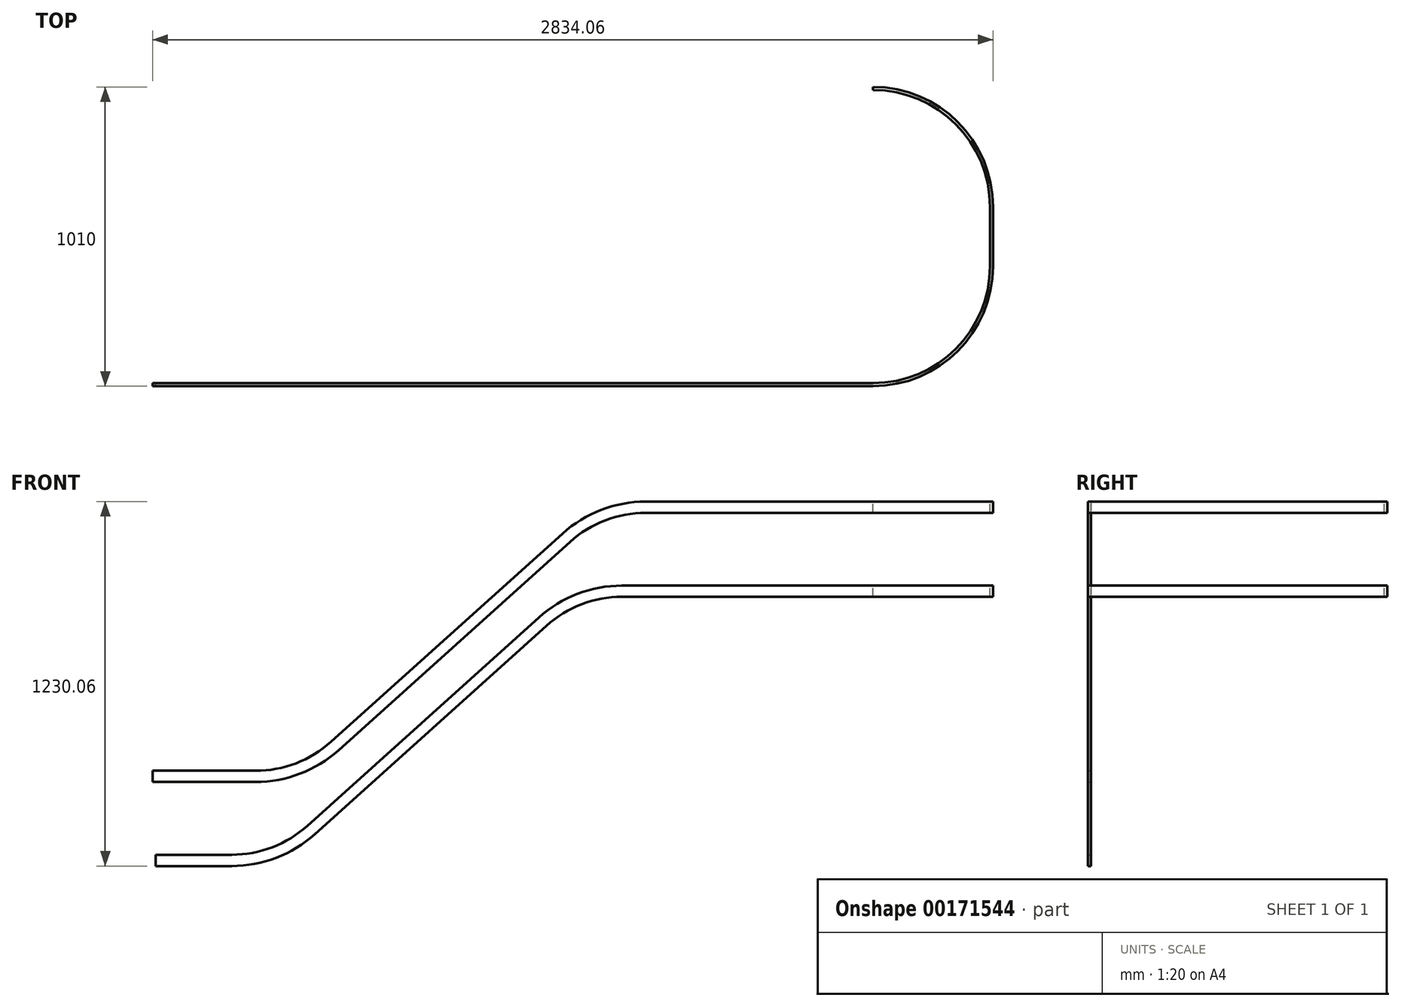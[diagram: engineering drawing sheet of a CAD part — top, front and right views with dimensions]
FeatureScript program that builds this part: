
annotation { "Feature Type Name" : "Feature", "Feature Type Description" : "" }
export const myFeature = defineFeature(function(context is Context, id is Id, definition is map)
    precondition{}
    {
        {
            var Q0;
            Q0=qCreatedBy(makeId("Front.planeOp"),FACE);
            var sketch = newSketch(context, id + "F0", { "sketchPlane" : qUnion([Q0])});
            skLineSegment(sketch, "E0", {"start": v(129.67, 109.8) * mm, "end": v(910.51, 812.88) * mm, "construction": true});
            skArc(sketch, "E1.0", {"start": v(1191.37, 1269.69) * mm, "mid": v(1191.37, 1269.69) * mm, "end": v(1191.36, 1269.69) * mm});
            skLineSegment(sketch, "E2", {"start": v(1191.36, 1269.69) * mm, "end": v(1191.37, 1269.69) * mm});
            skLineSegment(sketch, "E3", {"start": v(-404.44, 290.56) * mm, "end": v(-57.98, 290.56) * mm, "construction": true});
            skLineSegment(sketch, "E4", {"start": v(-394.44, 7.06) * mm, "end": v(-137.98, 7.06) * mm, "construction": true});
            skLineSegment(sketch, "E5", {"start": v(1178.16, 915.62) * mm, "end": v(2024.62, 915.62) * mm, "construction": true});
            skLineSegment(sketch, "E6", {"start": v(1258.16, 1199.12) * mm, "end": v(2024.62, 1199.12) * mm, "construction": true});
            skPoint(sketch, "E7", {"position": v(-404.44, 309.56) * mm});
            skPoint(sketch, "E8", {"position": v(-404.44, 271.56) * mm});
            skPoint(sketch, "E9", {"position": v(-394.44, 26.06) * mm});
            skPoint(sketch, "E10", {"position": v(-394.44, -11.94) * mm});
            skPoint(sketch, "E11", {"position": v(2024.62, 896.62) * mm});
            skPoint(sketch, "E12", {"position": v(2024.62, 934.62) * mm});
            skPoint(sketch, "E13.visualSharp", {"position": v(95.56, 290.56) * mm});
            skPoint(sketch, "E14.visualSharp", {"position": v(15.56, 7.06) * mm});
            skPoint(sketch, "E15.visualSharp", {"position": v(1024.62, 915.62) * mm});
            skPoint(sketch, "E16.visualSharp", {"position": v(1104.62, 1199.12) * mm});
            skLineSegment(sketch, "E17", {"start": v(-404.44, 271.56) * mm, "end": v(-404.44, 309.56) * mm});
            skLineSegment(sketch, "E18", {"start": v(-394.44, 26.06) * mm, "end": v(-394.44, -11.94) * mm});
            skLineSegment(sketch, "E19", {"start": v(2024.62, 896.62) * mm, "end": v(2024.62, 934.62) * mm});
            skLineSegment(sketch, "E20", {"start": v(572.56, 720.05) * mm, "end": v(572.56, 508.58) * mm, "construction": true});
            skLineSegment(sketch, "E21", {"start": v(209.67, 393.3) * mm, "end": v(990.51, 1096.38) * mm, "construction": true});
            skArc(sketch, "E22.filletArc", {"start": v(-137.98, 7.06) * mm, "mid": v(5.37, 33.63) * mm, "end": v(129.67, 109.8) * mm, "construction": true});
            skArc(sketch, "E23.filletArc", {"start": v(-57.98, 290.56) * mm, "mid": v(85.37, 317.13) * mm, "end": v(209.67, 393.3) * mm, "construction": true});
            skArc(sketch, "E24.filletArc", {"start": v(1178.16, 915.62) * mm, "mid": v(1034.82, 889.05) * mm, "end": v(910.51, 812.88) * mm, "construction": true});
            skArc(sketch, "E25.filletArc", {"start": v(1258.16, 1199.12) * mm, "mid": v(1114.82, 1172.55) * mm, "end": v(990.51, 1096.38) * mm, "construction": true});
            skArc(sketch, "E26.0", {"start": v(-137.98, -11.94) * mm, "mid": v(12.18, 15.9) * mm, "end": v(142.39, 95.69) * mm});
            skArc(sketch, "E27.0", {"start": v(-137.98, 26.06) * mm, "mid": v(-1.44, 51.37) * mm, "end": v(116.96, 123.93) * mm});
            skArc(sketch, "E28.0", {"start": v(1178.16, 934.62) * mm, "mid": v(1028, 906.8) * mm, "end": v(897.8, 827) * mm});
            skArc(sketch, "E29.0", {"start": v(1178.16, 896.62) * mm, "mid": v(1041.63, 871.31) * mm, "end": v(923.23, 798.76) * mm});
            skArc(sketch, "E30.0", {"start": v(1258.16, 1218.12) * mm, "mid": v(1108, 1190.3) * mm, "end": v(977.8, 1110.5) * mm});
            skArc(sketch, "E31.0", {"start": v(1258.16, 1180.12) * mm, "mid": v(1121.63, 1154.81) * mm, "end": v(1003.23, 1082.26) * mm});
            skArc(sketch, "E32.0", {"start": v(-57.98, 271.56) * mm, "mid": v(92.18, 299.4) * mm, "end": v(222.39, 379.19) * mm});
            skArc(sketch, "E33.0", {"start": v(-57.98, 309.56) * mm, "mid": v(78.56, 334.87) * mm, "end": v(196.96, 407.43) * mm});
            skLineSegment(sketch, "E34", {"start": v(-57.98, 271.56) * mm, "end": v(-404.44, 271.56) * mm});
            skLineSegment(sketch, "E35", {"start": v(-57.98, 309.56) * mm, "end": v(-404.44, 309.56) * mm});
            skLineSegment(sketch, "E36", {"start": v(222.39, 379.19) * mm, "end": v(1003.23, 1082.26) * mm});
            skLineSegment(sketch, "E37", {"start": v(196.96, 407.43) * mm, "end": v(977.8, 1110.5) * mm});
            skLineSegment(sketch, "E38", {"start": v(-137.98, -11.94) * mm, "end": v(-394.44, -11.94) * mm});
            skLineSegment(sketch, "E39", {"start": v(-394.44, 26.06) * mm, "end": v(-137.98, 26.06) * mm});
            skLineSegment(sketch, "E40", {"start": v(142.39, 95.69) * mm, "end": v(923.23, 798.76) * mm});
            skLineSegment(sketch, "E41", {"start": v(897.8, 827) * mm, "end": v(116.96, 123.93) * mm});
            skLineSegment(sketch, "E42", {"start": v(1178.16, 896.62) * mm, "end": v(2024.62, 896.62) * mm});
            skLineSegment(sketch, "E43", {"start": v(2024.62, 934.62) * mm, "end": v(1178.16, 934.62) * mm});
            skLineSegment(sketch, "E44", {"start": v(1258.16, 1180.12) * mm, "end": v(2024.62, 1180.12) * mm});
            skLineSegment(sketch, "E45", {"start": v(2024.62, 1218.12) * mm, "end": v(1258.16, 1218.12) * mm});
            skLineSegment(sketch, "E46", {"start": v(2024.62, 1180.12) * mm, "end": v(2024.62, 1218.12) * mm});
            skSolve(sketch);
        }
        {
            var Q0;
            Q0=qSketchRegion(id+"F0",true);
            extrude(context, id + "F1", {"entities" : qUnion([Q0]), "depth" : 10 * mm});
        }
        {
            var Q0;
            Q0=makeQuery(id+"F1.opExtrude","SWEPT_FACE",FACE,{"disambiguationData":[OSD([sQuery(id+"F0.wireOp",EDGE,"E45")])]});
            var sketch = newSketch(context, id + "F2", { "sketchPlane" : qUnion([Q0])});
            skLineSegment(sketch, "E47", {"start": v(2024.62, -5) * mm, "end": v(2024.62, 795) * mm, "construction": true});
            skArc(sketch, "E48", {"start": v(2024.62, -5) * mm, "mid": v(2307.46, 112.16) * mm, "end": v(2424.62, 395) * mm});
            skLineSegment(sketch, "E49", {"start": v(2024.62, 795) * mm, "end": v(2024.62, 995) * mm, "construction": true});
            skLineSegment(sketch, "E50", {"start": v(2424.62, 595) * mm, "end": v(2424.62, 995) * mm, "construction": true});
            skArc(sketch, "E51", {"start": v(2424.62, 595) * mm, "mid": v(2307.46, 877.84) * mm, "end": v(2024.62, 995) * mm});
            skPoint(sketch, "E51.second.point", {"position": v(2424.62, 595) * mm});
            skPoint(sketch, "E51.third.point", {"position": v(1768.82, 287.49) * mm});
            skLineSegment(sketch, "E52", {"start": v(2424.62, 595) * mm, "end": v(2424.62, 395) * mm});
            skSolve(sketch);
        }
        {
            var Q0;
            Q0=makeQuery(id+"F1.opExtrude","SWEPT_FACE",FACE,{"disambiguationData":[OSD([sQuery(id+"F0.wireOp",EDGE,"E46")])]});
            var Q1;
            Q1=sQuery(id+"F2.wireOp",EDGE,"E48");
            var Q2;
            Q2=sQuery(id+"F2.wireOp",EDGE,"E52");
            var Q3;
            Q3=sQuery(id+"F2.wireOp",EDGE,"E51");
            sweep(context, id + "F3", {"operationType" : NewBodyOperationType.ADD, "profiles" : qUnion([Q0]), "path" : qUnion([Q1, Q2, Q3])});
        }
        {
            var Q0;
            Q0=makeQuery(id+"F1.opExtrude","SWEPT_FACE",FACE,{"disambiguationData":[OSD([sQuery(id+"F0.wireOp",EDGE,"E42")])]});
            var sketch = newSketch(context, id + "F4", { "sketchPlane" : qUnion([Q0])});
            skLineSegment(sketch, "E53", {"start": v(2024.62, 5) * mm, "end": v(2024.62, -995) * mm, "construction": true});
            skArc(sketch, "E54", {"start": v(2424.62, -395) * mm, "mid": v(2307.46, -112.16) * mm, "end": v(2024.62, 5) * mm});
            skArc(sketch, "E55", {"start": v(2024.62, -995) * mm, "mid": v(2307.46, -877.84) * mm, "end": v(2424.62, -595) * mm});
            skLineSegment(sketch, "E56", {"start": v(2424.62, -395) * mm, "end": v(2424.62, -595) * mm});
            skSolve(sketch);
        }
        {
            var Q0;
            Q0=makeQuery(id+"F1.opExtrude","SWEPT_FACE",FACE,{"disambiguationData":[OSD([sQuery(id+"F0.wireOp",EDGE,"E19")])]});
            var Q1;
            Q1=sQuery(id+"F4.wireOp",EDGE,"E54");
            var Q2;
            Q2=sQuery(id+"F4.wireOp",EDGE,"E56");
            var Q3;
            Q3=sQuery(id+"F4.wireOp",EDGE,"E55");
            sweep(context, id + "F5", {"operationType" : NewBodyOperationType.ADD, "profiles" : qUnion([Q0]), "path" : qUnion([Q1, Q2, Q3])});
        }
    });
